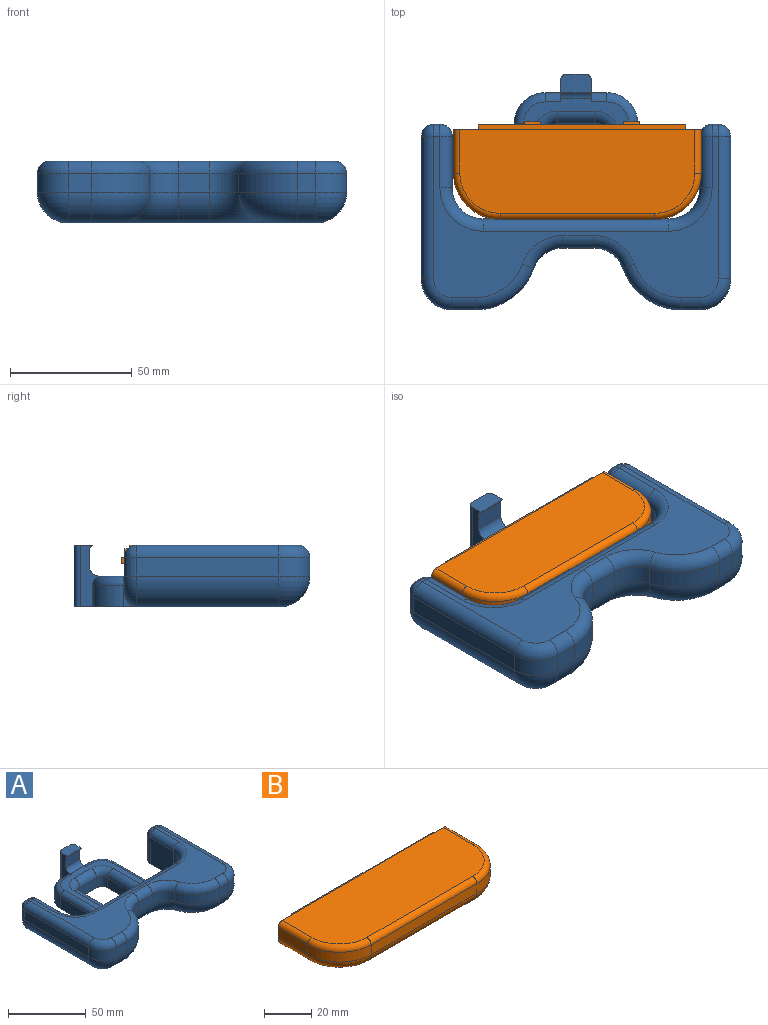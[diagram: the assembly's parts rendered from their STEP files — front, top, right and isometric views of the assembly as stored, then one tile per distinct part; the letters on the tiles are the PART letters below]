
ASSEMBLY  parts=2 mates=1
PART A: 93 faces, bbox 129.1x98.9x26.5 mm
  f0: plane 12.7x0.11mm, normal (0,-1,0), area 1.4mm2, adj f1,f50,f54,f90
  f1: plane 25.4x8.89mm, normal (1,0,0), area 119.9mm2, adj f0,f2,f3,f7,f54,f56,f67,f90
  f2: plane 49.28x43.18mm, normal (0,0,1), area 527.8mm2, adj f1,f4,f50,f62,f63,f64,f65,f66
  f3: plane 8.89x6.35mm, normal (0,1,0), area 56.5mm2, adj f1,f7,f53,f67
  f4: plane 76.2x20.32mm, normal (0,1,0), area 1242.7mm2, adj f2,f7,f8,f9,f10,f44,f45,f48
  f5: plane 13.3x2.54mm, normal (0,1,0), area 29.3mm2, adj f69,f70,f71,f73
  f6: plane 116.84x66.04mm, normal (0,0,1), area 2279.4mm2, adj f23,f24,f25,f26,f27,f28,f29,f30
  f7: plane 101.6x84.1mm, normal (0,0,-1), area 2890.5mm2, adj f1,f3,f4,f8,f10,f34,f36,f37
  f8: torus R=25.4mm, axis (0,0,1), area 422.2mm2, adj f4,f7,f9,f18,f37
  f9: cylinder r=12.7mm len=12.7mm, axis (1,0,0), area 244mm2, adj f4,f8,f10,f11
  f10: torus R=25.4mm, axis (0,0,1), area 422.2mm2, adj f4,f7,f9,f17,f38,f47
  f11: plane 12.7x7.62mm, normal (0,-1,0), area 96.8mm2, adj f9,f17,f18,f28
  f12: plane 58.42x7.62mm, normal (1,0,0), area 445.2mm2, adj f21,f33,f41,f75
  f13: plane 13.3x2.54mm, normal (0,1,0), area 29.3mm2, adj f75,f76,f77,f79
  f14: plane 58.42x7.62mm, normal (-1,0,0), area 445.2mm2, adj f22,f23,f34,f69
  f15: plane 9.48x7.62mm, normal (0,-1,0), area 72.2mm2, adj f20,f22,f25,f36
  f16: plane 7.62x7.58mm, normal (0,-1,0), area 57.7mm2, adj f19,f21,f31,f39
  f17: cylinder r=12.7mm len=11.97mm, axis (0,0,-1), area 119.1mm2, adj f10,f11,f19,f29
  f18: cylinder r=12.7mm len=11.97mm, axis (0,0,1), area 119.1mm2, adj f8,f11,f20,f27
  f19: cylinder r=25.4mm len=23.95mm, axis (0,0,-1), area 238.2mm2, adj f16,f17,f30,f38
  f20: cylinder r=25.4mm len=23.95mm, axis (0,0,1), area 238.2mm2, adj f15,f18,f26,f37
  f21: cylinder r=12.7mm len=12.7mm, axis (0,0,-1), area 152mm2, adj f12,f16,f32,f40
  f22: cylinder r=12.7mm len=12.7mm, axis (0,0,1), area 152mm2, adj f14,f15,f24,f35
  f23: cylinder r=5.08mm len=58.42mm, axis (0,1,0), area 466.2mm2, adj f6,f14,f24,f68
  f24: torus R=7.62mm, axis (0,0,1), area 136mm2, adj f6,f22,f23,f25
  f25: cylinder r=5.08mm len=9.48mm, axis (-1,0,0), area 75.7mm2, adj f6,f15,f24,f26
  f26: torus R=20.32mm, axis (0,0,1), area 231.4mm2, adj f6,f20,f25,f27
  f27: torus R=17.78mm, axis (0,0,1), area 142.9mm2, adj f6,f18,f26,f28
  f28: cylinder r=5.08mm len=12.7mm, axis (-1,0,0), area 101.3mm2, adj f6,f11,f27,f29
  f29: torus R=17.78mm, axis (0,0,1), area 142.9mm2, adj f6,f17,f28,f30
  f30: torus R=20.32mm, axis (0,0,1), area 231.4mm2, adj f6,f19,f29,f31
  f31: cylinder r=5.08mm len=7.58mm, axis (-1,0,0), area 60.5mm2, adj f6,f16,f30,f32
  f32: torus R=7.62mm, axis (0,0,1), area 136mm2, adj f6,f21,f31,f33
  f33: cylinder r=5.08mm len=58.42mm, axis (0,-1,0), area 466.2mm2, adj f6,f12,f32,f74
  f34: cylinder r=12.7mm len=58.42mm, axis (0,-1,0), area 1165.4mm2, adj f7,f14,f35,f42,f71
  f35: sphere r=12.7mm, area 253.4mm2, adj f22,f34,f36
  f36: cylinder r=12.7mm len=12.7mm, axis (1,0,0), area 189.1mm2, adj f7,f15,f35,f37
  f37: torus R=12.7mm, axis (0,0,1), area 510.4mm2, adj f7,f8,f20,f36
  f38: torus R=12.7mm, axis (0,0,1), area 510.4mm2, adj f7,f10,f19,f39
  f39: cylinder r=12.7mm len=12.7mm, axis (1,0,0), area 151.2mm2, adj f7,f16,f38,f40
  f40: sphere r=12.7mm, area 253.4mm2, adj f21,f39,f41
  f41: cylinder r=12.7mm len=58.42mm, axis (0,1,0), area 1165.4mm2, adj f7,f12,f40,f43,f77
  f42: plane 21.06x20.32mm, normal (1,0,0), area 427.9mm2, adj f34,f48,f57,f73
  f43: plane 21.06x20.32mm, normal (-1,0,0), area 427.9mm2, adj f41,f49,f61,f79
  f44: plane 39.12x8.89mm, normal (-1,0,0), area 347.7mm2, adj f4,f7,f52,f62
  f45: plane 39.12x8.89mm, normal (1,0,0), area 347.7mm2, adj f4,f7,f53,f65
  f46: plane 8.89x6.35mm, normal (0,1,0), area 56.5mm2, adj f7,f50,f52,f64
  f47: plane 0.68x0.01mm, normal (0,-1,0), area 0mm2, adj f7,f10,f82
  f48: cylinder r=12.7mm len=20.32mm, axis (0,0,1), area 405.4mm2, adj f4,f7,f42,f58
  f49: cylinder r=12.7mm len=20.32mm, axis (0,0,-1), area 405.4mm2, adj f4,f7,f43,f60
  f50: plane 25.4x8.89mm, normal (-1,0,0), area 119.9mm2, adj f0,f2,f7,f46,f54,f55,f64,f90
  f51: plane 25.4x7.62mm, normal (0,1,0), area 193.5mm2, adj f7,f54,f55,f56
  f52: cylinder r=12.7mm len=12.7mm, axis (0,0,-1), area 177.3mm2, adj f7,f44,f46,f63
  f53: cylinder r=12.7mm len=12.7mm, axis (0,0,1), area 177.3mm2, adj f3,f7,f45,f66
  f54: plane 12.7x7.62mm, normal (0,0,1), area 94mm2, adj f0,f1,f50,f51,f55,f56
  f55: cylinder r=2.54mm len=25.4mm, axis (0,0,-1), area 101.3mm2, adj f7,f50,f51,f54
  f56: cylinder r=2.54mm len=25.4mm, axis (0,0,1), area 101.3mm2, adj f1,f7,f51,f54
  f57: cylinder r=5.08mm len=21.06mm, axis (0,-1,0), area 168mm2, adj f6,f42,f58,f72
  f58: torus R=17.78mm, axis (0,0,1), area 182.3mm2, adj f6,f48,f57,f59
  f59: cylinder r=5.08mm len=76.2mm, axis (-1,0,0), area 608mm2, adj f4,f6,f58,f60
  f60: torus R=17.78mm, axis (0,0,1), area 182.3mm2, adj f6,f49,f59,f61
  f61: cylinder r=5.08mm len=21.06mm, axis (0,1,0), area 168mm2, adj f6,f43,f60,f78
  f62: cylinder r=3.81mm len=39.12mm, axis (0,-1,0), area 234.1mm2, adj f2,f4,f44,f63
  f63: torus R=8.89mm, axis (0,0,-1), area 106.4mm2, adj f2,f52,f62,f64
  f64: cylinder r=3.81mm len=6.35mm, axis (-1,0,0), area 38mm2, adj f2,f46,f50,f63
  f65: cylinder r=3.81mm len=39.12mm, axis (0,1,0), area 234.1mm2, adj f2,f4,f45,f66
  f66: torus R=8.89mm, axis (0,0,-1), area 106.4mm2, adj f2,f53,f65,f67
  f67: cylinder r=3.81mm len=6.35mm, axis (-1,0,0), area 38mm2, adj f1,f2,f3,f66
  f68: sphere r=5.08mm, area 40.5mm2, adj f23,f69,f70
  f69: cylinder r=5.08mm len=7.62mm, axis (0,0,-1), area 60.8mm2, adj f5,f14,f68,f71
  f70: cylinder r=5.08mm len=5.08mm, axis (1,0,0), area 20.3mm2, adj f5,f6,f68,f72
  f71: torus R=7.62mm, axis (0,-1,0), area 120.9mm2, adj f5,f34,f69,f73
  f72: sphere r=5.08mm, area 40.5mm2, adj f57,f70,f73
  f73: cylinder r=5.08mm len=20.32mm, axis (0,0,1), area 144.6mm2, adj f5,f42,f71,f72
  f74: sphere r=5.08mm, area 40.5mm2, adj f33,f75,f76
  f75: cylinder r=5.08mm len=7.62mm, axis (0,0,1), area 60.8mm2, adj f12,f13,f74,f77
  f76: cylinder r=5.08mm len=5.08mm, axis (1,0,0), area 20.3mm2, adj f6,f13,f74,f78
  f77: torus R=7.62mm, axis (0,-1,0), area 120.9mm2, adj f13,f41,f75,f79
  f78: sphere r=5.08mm, area 40.5mm2, adj f61,f76,f79
  f79: cylinder r=5.08mm len=20.32mm, axis (0,0,-1), area 144.6mm2, adj f13,f43,f77,f78
  f80: plane 34.04x7.62mm, normal (1,0,0), area 259.4mm2, adj f4,f7,f83,f84
  f81: plane 15.24x7.62mm, normal (0,-1,0), area 116.1mm2, adj f7,f83,f86,f89
  f82: plane 34.04x7.62mm, normal (-1,0,0), area 259.4mm2, adj f4,f7,f47,f87,f89
  f83: cylinder r=5.08mm len=7.62mm, axis (0,0,-1), area 60.8mm2, adj f7,f80,f81,f85
  f84: cylinder r=5.08mm len=34.04mm, axis (0,-1,0), area 271.6mm2, adj f2,f4,f80,f85
  f85: torus R=10.16mm, axis (0,0,-1), area 86.8mm2, adj f2,f83,f84,f86
  f86: cylinder r=5.08mm len=15.24mm, axis (-1,0,0), area 121.6mm2, adj f2,f81,f85,f88
  f87: cylinder r=5.08mm len=34.04mm, axis (0,1,0), area 271.6mm2, adj f2,f4,f82,f88
  f88: torus R=10.16mm, axis (0,0,-1), area 86.8mm2, adj f2,f86,f87,f89
  f89: cylinder r=5.08mm len=7.62mm, axis (0,0,1), area 60.8mm2, adj f7,f81,f82,f88
  f90: cylinder r=1.91mm len=12.7mm, axis (-1,0,0), area 29.8mm2, adj f0,f1,f50,f91
  f91: plane 12.7x6.99mm, normal (0,-1,0), area 88.7mm2, adj f1,f50,f90,f92
  f92: cylinder r=3.81mm len=12.7mm, axis (-1,0,0), area 76mm2, adj f1,f2,f50,f91
PART B: 33 faces, bbox 104.7x41.7x12.7 mm
  f0: plane 85.09x9.7mm, normal (0,1,0), area 793.1mm2, adj f14,f15,f16,f17,f23,f24,f25,f26
  f1: plane 101.6x12.7mm, normal (0,1,0), area 451.1mm2, adj f2,f4,f5,f6,f9,f13,f14,f15
  f2: plane 17.78x5.08mm, normal (-1,0,0), area 90.3mm2, adj f1,f7,f9,f18
  f3: plane 63.5x5.08mm, normal (0,-1,0), area 322.6mm2, adj f7,f8,f11,f20
  f4: plane 17.78x5.08mm, normal (1,0,0), area 90.3mm2, adj f1,f8,f13,f22
  f5: plane 96.52x34.29mm, normal (0,0,1), area 3192.7mm2, adj f1,f18,f19,f20,f21,f22
  f6: plane 91.44x31.75mm, normal (0,0,-1), area 2819.5mm2, adj f1,f9,f10,f11,f12,f13
  f7: cylinder r=19.05mm len=19.05mm, axis (0,0,-1), area 152mm2, adj f2,f3,f10,f19
  f8: cylinder r=19.05mm len=19.05mm, axis (0,0,1), area 152mm2, adj f3,f4,f12,f21
  f9: cylinder r=5.08mm len=17.78mm, axis (0,-1,0), area 141.9mm2, adj f1,f2,f6,f10
  f10: torus R=13.97mm, axis (0,0,1), area 215.6mm2, adj f6,f7,f9,f11
  f11: cylinder r=5.08mm len=63.5mm, axis (1,0,0), area 506.7mm2, adj f3,f6,f10,f12
  f12: torus R=13.97mm, axis (0,0,1), area 215.6mm2, adj f6,f8,f11,f13
  f13: cylinder r=5.08mm len=17.78mm, axis (0,1,0), area 141.9mm2, adj f1,f4,f6,f12
  f14: plane 85.09x2mm, normal (0,0,1), area 170.2mm2, adj f0,f1,f15,f17
  f15: plane 9.7x2mm, normal (1,0,0), area 19.4mm2, adj f0,f1,f14,f16
  f16: plane 85.09x2mm, normal (0,0,-1), area 170.2mm2, adj f0,f1,f15,f17
  f17: plane 9.7x2mm, normal (-1,0,0), area 19.4mm2, adj f0,f1,f14,f16
  f18: cylinder r=2.54mm len=17.78mm, axis (0,1,0), area 70.9mm2, adj f1,f2,f5,f19
  f19: torus R=16.51mm, axis (0,0,1), area 113.6mm2, adj f5,f7,f18,f20
  f20: cylinder r=2.54mm len=63.5mm, axis (-1,0,0), area 253.4mm2, adj f3,f5,f19,f21
  f21: torus R=16.51mm, axis (0,0,1), area 113.6mm2, adj f5,f8,f20,f22
  f22: cylinder r=2.54mm len=17.78mm, axis (0,-1,0), area 70.9mm2, adj f1,f4,f5,f21
  f23: plane 2.54x1.27mm, normal (1,0,0), area 3.2mm2, adj f0,f24,f26,f27
  f24: plane 6.35x1.27mm, normal (0,0,-1), area 8.1mm2, adj f0,f23,f25,f27
  f25: plane 2.54x1.27mm, normal (-1,0,0), area 3.2mm2, adj f0,f24,f26,f27
  f26: plane 6.35x1.27mm, normal (0,0,1), area 8.1mm2, adj f0,f23,f25,f27
  f27: plane 6.35x2.54mm, normal (0,1,0), area 16.1mm2, adj f23,f24,f25,f26
  f28: plane 6.35x1.27mm, normal (0,0,-1), area 8.1mm2, adj f0,f29,f31,f32
  f29: plane 2.54x1.27mm, normal (-1,0,0), area 3.2mm2, adj f0,f28,f30,f32
  f30: plane 6.35x1.27mm, normal (0,0,1), area 8.1mm2, adj f0,f29,f31,f32
  f31: plane 2.54x1.27mm, normal (1,0,0), area 3.2mm2, adj f0,f28,f30,f32
  f32: plane 6.35x2.54mm, normal (0,1,0), area 16.1mm2, adj f28,f29,f30,f31
PLACE A t=(-1.67,-7.74,-19.7)mm fixed
PLACE B t=(-1.1,-3.02,-19.7)mm
MATE planar B.f6 <-> A.f2  axis (0,0,-1) through (-1.1,-0.1,-19.7)mm
